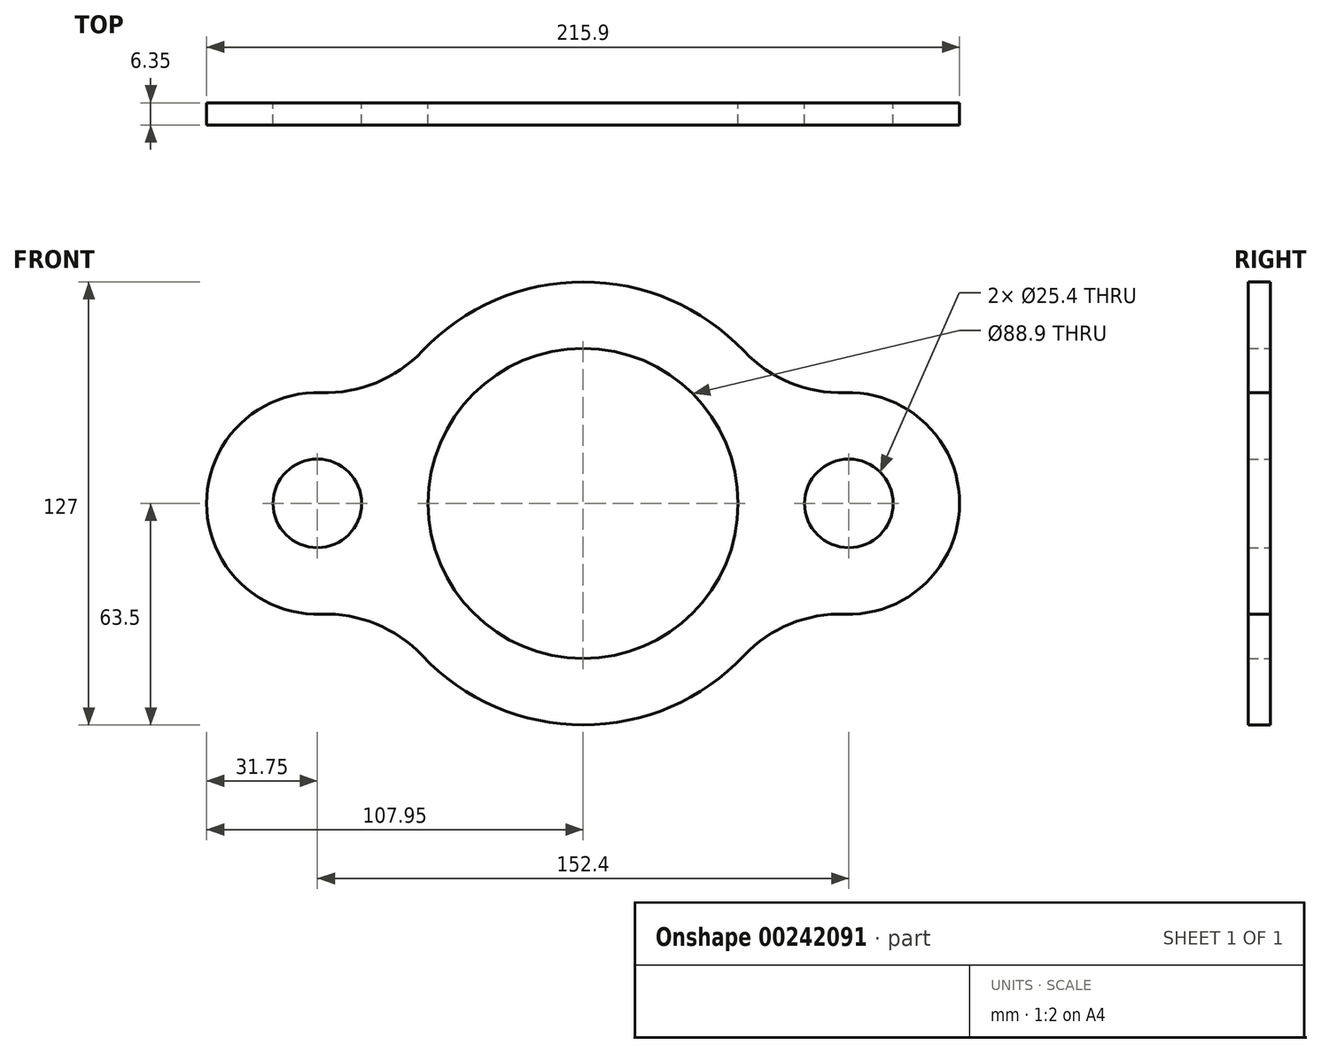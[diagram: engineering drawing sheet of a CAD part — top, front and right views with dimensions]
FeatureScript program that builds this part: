
annotation { "Feature Type Name" : "Feature", "Feature Type Description" : "" }
export const myFeature = defineFeature(function(context is Context, id is Id, definition is map)
    precondition{}
    {
        {
            var Q0;
            Q0=qCreatedBy(makeId("Front.planeOp"),FACE);
            var sketch = newSketch(context, id + "F0", { "sketchPlane" : qUnion([Q0])});
            skArc(sketch, "E0", {"start": v(-46.14, -43.63) * mm, "mid": v(0, -63.5) * mm, "end": v(46.14, -43.63) * mm});
            skArc(sketch, "E1", {"start": v(75.12, -31.73) * mm, "mid": v(107.95, 0) * mm, "end": v(75.12, 31.73) * mm});
            skArc(sketch, "E2", {"start": v(-75.12, 31.73) * mm, "mid": v(-107.95, 0) * mm, "end": v(-75.12, -31.73) * mm});
            skCircle(sketch, "E3", {"center": v(0, 0) * mm, "radius": 44.45 * mm});
            skCircle(sketch, "E4", {"center": v(-76.2, 0) * mm, "radius": 12.7 * mm});
            skCircle(sketch, "E5", {"center": v(76.2, 0) * mm, "radius": 12.7 * mm});
            skArc(sketch, "E6.trimOffspring", {"start": v(46.14, 43.63) * mm, "mid": v(0, 63.5) * mm, "end": v(-46.14, 43.63) * mm});
            skPoint(sketch, "E7.visualSharp", {"position": v(-57.94, 25.98) * mm});
            skArc(sketch, "E7.filletArc", {"start": v(-75.12, 31.73) * mm, "mid": v(-59.35, 34.56) * mm, "end": v(-46.14, 43.63) * mm});
            skPoint(sketch, "E8.visualSharp", {"position": v(57.94, 25.98) * mm});
            skArc(sketch, "E8.filletArc", {"start": v(46.14, 43.63) * mm, "mid": v(59.35, 34.56) * mm, "end": v(75.12, 31.73) * mm});
            skPoint(sketch, "E9.visualSharp", {"position": v(57.94, -25.98) * mm});
            skArc(sketch, "E9.filletArc", {"start": v(75.12, -31.73) * mm, "mid": v(59.35, -34.56) * mm, "end": v(46.14, -43.63) * mm});
            skPoint(sketch, "E10.visualSharp", {"position": v(-57.94, -25.98) * mm});
            skArc(sketch, "E10.filletArc", {"start": v(-46.14, -43.63) * mm, "mid": v(-59.35, -34.56) * mm, "end": v(-75.12, -31.73) * mm});
            skSolve(sketch);
        }
        {
            var Q0;
            Q0=makeQuery(id+"F0.imprint","IMPRINT",FACE,{"disambiguationData":[TD([[makeQuery(id+"F0.imprint","IMPRINT",EDGE,{"derivedFrom":sQuery(id+"F0.wireOp",EDGE,"E0")}),1.0]])]});
            extrude(context, id + "F1", {"entities" : qUnion([Q0]), "depth" : 6.35 * mm});
        }
    });
